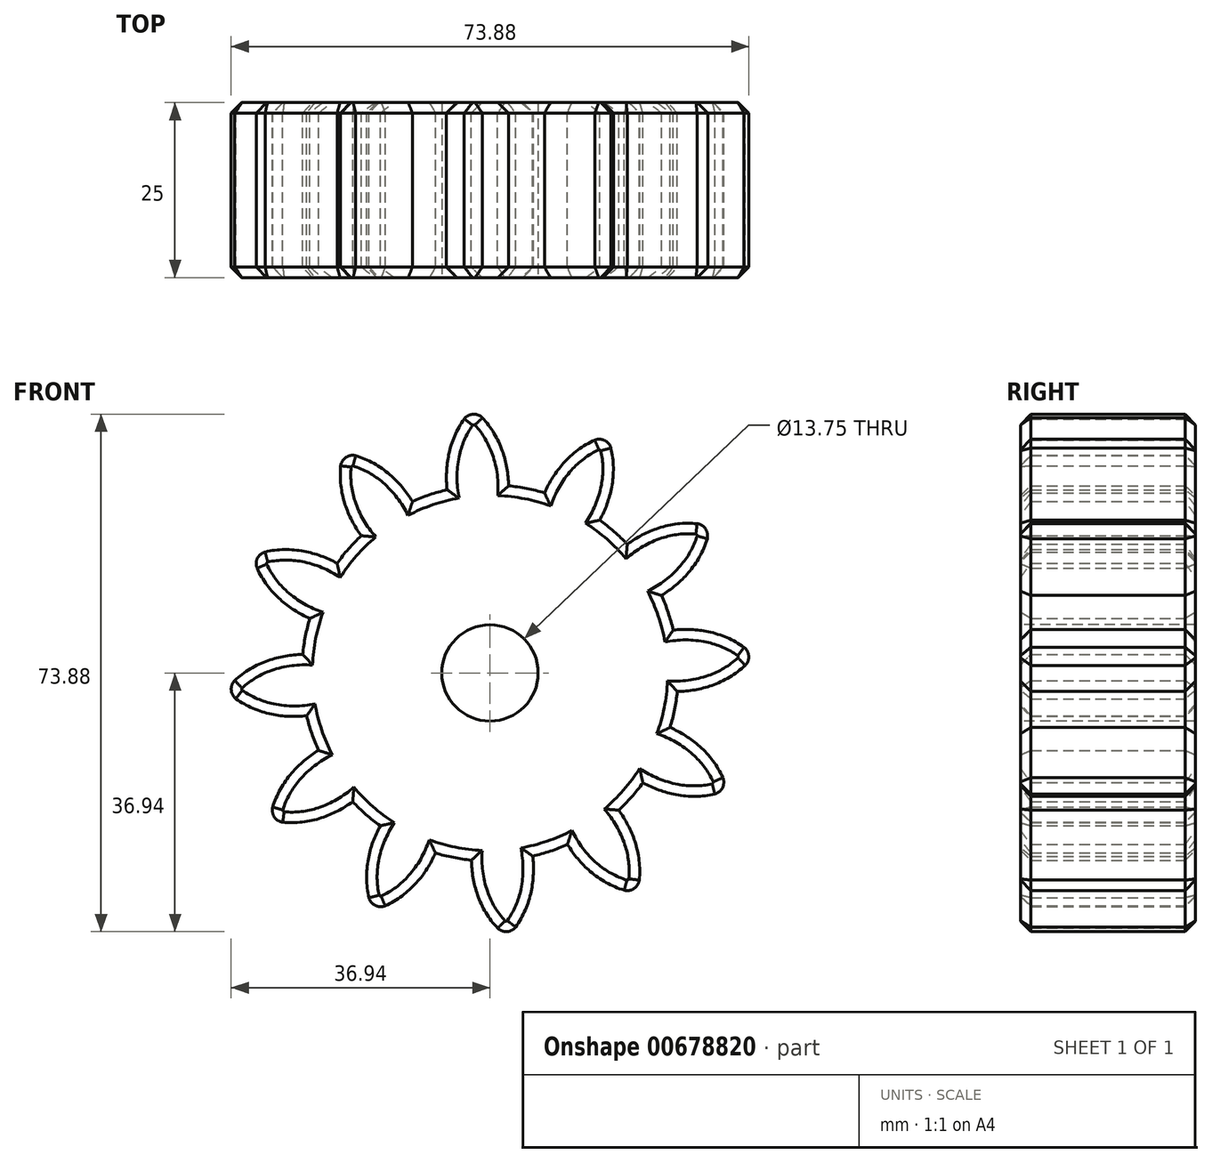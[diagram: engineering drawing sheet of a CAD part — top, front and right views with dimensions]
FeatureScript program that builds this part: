
annotation { "Feature Type Name" : "Feature", "Feature Type Description" : "" }
export const myFeature = defineFeature(function(context is Context, id is Id, definition is map)
    precondition{}
    {
        {
            var Q0;
            Q0=qCreatedBy(makeId("Front.planeOp"),FACE);
            var sketch = newSketch(context, id + "F0", { "sketchPlane" : qUnion([Q0])});
            skCircle(sketch, "E0", {"center": v(0, 0) * mm, "radius": 26.86 * mm});
            skCircle(sketch, "E1", {"center": v(0, 0) * mm, "radius": 29.34 * mm, "construction": true});
            skCircle(sketch, "E2", {"center": v(0, 0) * mm, "radius": 31.75 * mm, "construction": true});
            skLineSegment(sketch, "E3", {"start": v(0, 0) * mm, "end": v(0, 90.28) * mm, "construction": true});
            skLineSegment(sketch, "E4", {"start": v(0, 0) * mm, "end": v(-5.89, 89.83) * mm, "construction": true});
            skLineSegment(sketch, "E5", {"start": v(0, 29.34) * mm, "end": v(-86.47, -2.14) * mm, "construction": true});
            skLineSegment(sketch, "E6", {"start": v(0, 29.34) * mm, "end": v(-89.07, 29.34) * mm, "construction": true});
            skCircle(sketch, "E7", {"center": v(0, 0) * mm, "radius": 27.57 * mm, "construction": true});
            skArc(sketch, "E8.MirrorCS", {"start": v(-4.16, 26.54) * mm, "mid": v(-4.05, 27.82) * mm, "end": v(-3.83, 29.09) * mm});
            skArc(sketch, "E9.MirrorCS", {"start": v(0.88, 53.71) * mm, "mid": v(0.64, 56.23) * mm, "end": v(0, 58.67) * mm});
            skArc(sketch, "E10", {"start": v(1.77, 31.68) * mm, "mid": v(0.6, 34.2) * mm, "end": v(-1.08, 36.44) * mm});
            skArc(sketch, "E11", {"start": v(2.65, 26.72) * mm, "mid": v(2.41, 29.23) * mm, "end": v(1.77, 31.68) * mm});
            skArc(sketch, "E12.MirrorCS", {"start": v(-6.11, 26.14) * mm, "mid": v(-6.2, 28.67) * mm, "end": v(-5.88, 31.17) * mm});
            skArc(sketch, "E13.MirrorCS", {"start": v(-5.88, 31.17) * mm, "mid": v(-5.04, 33.84) * mm, "end": v(-3.67, 36.27) * mm});
            skArc(sketch, "E14", {"start": v(-1.08, 36.44) * mm, "mid": v(-2.42, 36.94) * mm, "end": v(-3.67, 36.27) * mm});
            skSolve(sketch);
        }
        {
            var Q0;
            {var subQ0=sQuery(id+"F0.wireOp",EDGE,"E0");var subQ1=makeQuery(id+"F0.imprint","IMPRINT",VERTEX,{"derivedFrom":subQ0});Q0=makeQuery(id+"F0.imprint","IMPRINT",FACE,{"disambiguationData":[TD([[makeQuery(id+"F0.imprint","IMPRINT",EDGE,{"disambiguationData":[TD([[subQ1,1.0]])],"derivedFrom":subQ0}),1.0]])]});}
            var Q1;
            {var subQ1=sQuery(id+"F0.wireOp",EDGE,"E10");Q1=makeQuery(id+"F0.imprint","IMPRINT",FACE,{"disambiguationData":[TD([[makeQuery(id+"F0.imprint","IMPRINT",EDGE,{"derivedFrom":subQ1}),1.0]])]});}
            extrude(context, id + "F1", {"entities" : qUnion([Q0, Q1]), "depth" : 25 * mm, "offsetDistance" : 25 * mm});
        }
        {
            var Q0;
            Q0=makeQuery(id+"F1.opExtrude","SWEPT_BODY",BODY,{"disambiguationData":[OSD([sQuery(id+"F0.wireOp",EDGE,"E0"),sQuery(id+"F0.wireOp",EDGE,"y96EtzkA-fjPU-x1jf-0drD-OjpyX9tFYvnI"),sQuery(id+"F0.wireOp",EDGE,"724908ac-0687-431e-9ec8-69ff59eacf590.MirrorCS"),sQuery(id+"F0.wireOp",EDGE,"2490555c-e21d-4882-9143-33f16a250a770.MirrorCS"),sQuery(id+"F0.wireOp",EDGE,"E9.MirrorCS"),sQuery(id+"F0.wireOp",EDGE,"36OtFxwo-qp6n-tRVQ-woUy-RZQLZs2DcdZ9")])]});
            var Q1;
            Q1=makeQuery(id+"F1.opExtrude","SWEPT_FACE",FACE,{"disambiguationData":[OSD([sQuery(id+"F0.wireOp",EDGE,"E0")])]});
            circularPattern(context, id + "F2", {"operationType" : NewBodyOperationType.ADD, "entities" : qUnion([Q0]), "axis" : qUnion([Q1]), "angle" : 360 * degree, "instanceCount" : 12, "equalSpace" : true});
        }
        {
            var Q0;
            {var subQ0=makeQuery(id+"F1.opExtrude","CAP_FACE",FACE,{"disambiguationData":[OSD([sQuery(id+"F0.wireOp",EDGE,"E0"),sQuery(id+"F0.wireOp",EDGE,"ff6eb029-c4d1-4e66-88d8-c976b3e35ee2"),sQuery(id+"F0.wireOp",EDGE,"efe03a6d-2041-45f7-a397-e819af93c517.MirrorCS"),sQuery(id+"F0.wireOp",EDGE,"07d544c5-b1d6-4791-a01d-7e331bac1fb8.MirrorCS"),sQuery(id+"F0.wireOp",EDGE,"765999fa-03c8-4684-b91f-6193e64bcbe9.MirrorCS"),sQuery(id+"F0.wireOp",EDGE,"e1cfb975-41cf-48b3-ada3-c5f54a61fce5")])],"isStart":false});Q0=makeQuery(id+"F2.boolean.opBoolean","MERGE",FACE,{"derivedFrom":[subQ0,makeQuery(id+"F2.opPattern","COPY",FACE,{"derivedFrom":subQ0,"instanceName":"1"}),makeQuery(id+"F2.opPattern","COPY",FACE,{"derivedFrom":subQ0,"instanceName":"2"}),makeQuery(id+"F2.opPattern","COPY",FACE,{"derivedFrom":subQ0,"instanceName":"3"}),makeQuery(id+"F2.opPattern","COPY",FACE,{"derivedFrom":subQ0,"instanceName":"4"}),makeQuery(id+"F2.opPattern","COPY",FACE,{"derivedFrom":subQ0,"instanceName":"5"}),makeQuery(id+"F2.opPattern","COPY",FACE,{"derivedFrom":subQ0,"instanceName":"6"}),makeQuery(id+"F2.opPattern","COPY",FACE,{"derivedFrom":subQ0,"instanceName":"7"}),makeQuery(id+"F2.opPattern","COPY",FACE,{"derivedFrom":subQ0,"instanceName":"8"}),makeQuery(id+"F2.opPattern","COPY",FACE,{"derivedFrom":subQ0,"instanceName":"9"}),makeQuery(id+"F2.opPattern","COPY",FACE,{"derivedFrom":subQ0,"instanceName":"10"}),makeQuery(id+"F2.opPattern","COPY",FACE,{"derivedFrom":subQ0,"instanceName":"11"})]});}
            var Q1;
            Q1=makeQuery(id+"F2.opPattern","COPY",EDGE,{"derivedFrom":makeQuery(id+"F1.opExtrude","CAP_EDGE",EDGE,{"disambiguationData":[OSD([sQuery(id+"F0.wireOp",EDGE,"07d544c5-b1d6-4791-a01d-7e331bac1fb8.MirrorCS")])],"isStart":false}),"instanceName":"11"});
            var Q2;
            Q2=makeQuery(id+"F2.opPattern","COPY",EDGE,{"derivedFrom":makeQuery(id+"F1.opExtrude","CAP_EDGE",EDGE,{"disambiguationData":[OSD([sQuery(id+"F0.wireOp",EDGE,"efe03a6d-2041-45f7-a397-e819af93c517.MirrorCS")])],"isStart":false}),"instanceName":"11"});
            var Q3;
            Q3=makeQuery(id+"F2.opPattern","COPY",EDGE,{"derivedFrom":makeQuery(id+"F1.opExtrude","CAP_EDGE",EDGE,{"disambiguationData":[OSD([sQuery(id+"F0.wireOp",EDGE,"ff6eb029-c4d1-4e66-88d8-c976b3e35ee2")])],"isStart":false}),"instanceName":"11"});
            var Q4;
            Q4=makeQuery(id+"F2.opPattern","COPY",EDGE,{"derivedFrom":makeQuery(id+"F1.opExtrude","CAP_EDGE",EDGE,{"disambiguationData":[OSD([sQuery(id+"F0.wireOp",EDGE,"765999fa-03c8-4684-b91f-6193e64bcbe9.MirrorCS")])],"isStart":false}),"instanceName":"11"});
            var Q5;
            {var subQ0=makeQuery(id+"F1.opExtrude","CAP_FACE",FACE,{"disambiguationData":[OSD([sQuery(id+"F0.wireOp",EDGE,"E0"),sQuery(id+"F0.wireOp",EDGE,"E10"),sQuery(id+"F0.wireOp",EDGE,"E11"),sQuery(id+"F0.wireOp",EDGE,"E12.MirrorCS"),sQuery(id+"F0.wireOp",EDGE,"E13.MirrorCS"),sQuery(id+"F0.wireOp",EDGE,"E14")])],"isStart":true});Q5=makeQuery(id+"F2.boolean.opBoolean","MERGE",FACE,{"derivedFrom":[subQ0,makeQuery(id+"F2.opPattern","COPY",FACE,{"derivedFrom":subQ0,"instanceName":"1"}),makeQuery(id+"F2.opPattern","COPY",FACE,{"derivedFrom":subQ0,"instanceName":"2"}),makeQuery(id+"F2.opPattern","COPY",FACE,{"derivedFrom":subQ0,"instanceName":"3"}),makeQuery(id+"F2.opPattern","COPY",FACE,{"derivedFrom":subQ0,"instanceName":"4"}),makeQuery(id+"F2.opPattern","COPY",FACE,{"derivedFrom":subQ0,"instanceName":"5"}),makeQuery(id+"F2.opPattern","COPY",FACE,{"derivedFrom":subQ0,"instanceName":"6"}),makeQuery(id+"F2.opPattern","COPY",FACE,{"derivedFrom":subQ0,"instanceName":"7"}),makeQuery(id+"F2.opPattern","COPY",FACE,{"derivedFrom":subQ0,"instanceName":"8"}),makeQuery(id+"F2.opPattern","COPY",FACE,{"derivedFrom":subQ0,"instanceName":"9"}),makeQuery(id+"F2.opPattern","COPY",FACE,{"derivedFrom":subQ0,"instanceName":"10"}),makeQuery(id+"F2.opPattern","COPY",FACE,{"derivedFrom":subQ0,"instanceName":"11"})]});}
            chamfer(context, id + "F3", {"entities" : qUnion([Q0, Q1, Q2, Q3, Q4, Q5]), "width" : 1.5 * mm, "tangentPropagation" : true});
        }
        {
            var Q0;
            {var subQ0=makeQuery(id+"F1.opExtrude","CAP_FACE",FACE,{"disambiguationData":[OSD([sQuery(id+"F0.wireOp",EDGE,"E0"),sQuery(id+"F0.wireOp",EDGE,"E10"),sQuery(id+"F0.wireOp",EDGE,"E11"),sQuery(id+"F0.wireOp",EDGE,"E12.MirrorCS"),sQuery(id+"F0.wireOp",EDGE,"E13.MirrorCS"),sQuery(id+"F0.wireOp",EDGE,"E14")])],"isStart":false});Q0=makeQuery(id+"F2.boolean.opBoolean","MERGE",FACE,{"derivedFrom":[subQ0,makeQuery(id+"F2.opPattern","COPY",FACE,{"derivedFrom":subQ0,"instanceName":"1"}),makeQuery(id+"F2.opPattern","COPY",FACE,{"derivedFrom":subQ0,"instanceName":"2"}),makeQuery(id+"F2.opPattern","COPY",FACE,{"derivedFrom":subQ0,"instanceName":"3"}),makeQuery(id+"F2.opPattern","COPY",FACE,{"derivedFrom":subQ0,"instanceName":"4"}),makeQuery(id+"F2.opPattern","COPY",FACE,{"derivedFrom":subQ0,"instanceName":"5"}),makeQuery(id+"F2.opPattern","COPY",FACE,{"derivedFrom":subQ0,"instanceName":"6"}),makeQuery(id+"F2.opPattern","COPY",FACE,{"derivedFrom":subQ0,"instanceName":"7"}),makeQuery(id+"F2.opPattern","COPY",FACE,{"derivedFrom":subQ0,"instanceName":"8"}),makeQuery(id+"F2.opPattern","COPY",FACE,{"derivedFrom":subQ0,"instanceName":"9"}),makeQuery(id+"F2.opPattern","COPY",FACE,{"derivedFrom":subQ0,"instanceName":"10"}),makeQuery(id+"F2.opPattern","COPY",FACE,{"derivedFrom":subQ0,"instanceName":"11"})]});}
            var sketch = newSketch(context, id + "F4", { "sketchPlane" : qUnion([Q0])});
            skCircle(sketch, "E15", {"center": v(0, 0) * mm, "radius": 6.88 * mm});
            skSolve(sketch);
        }
        {
            var Q0;
            Q0=makeQuery(id+"F4.imprint","IMPRINT",FACE,{"disambiguationData":[TD([[makeQuery(id+"F4.imprint","IMPRINT",EDGE,{"derivedFrom":sQuery(id+"F4.wireOp",EDGE,"E15")}),1.0]])]});
            extrude(context, id + "F5", {"entities" : qUnion([Q0]), "operationType" : NewBodyOperationType.REMOVE, "oppositeDirection" : true, "depth" : 30 * mm, "offsetDistance" : 25 * mm});
        }
    });
